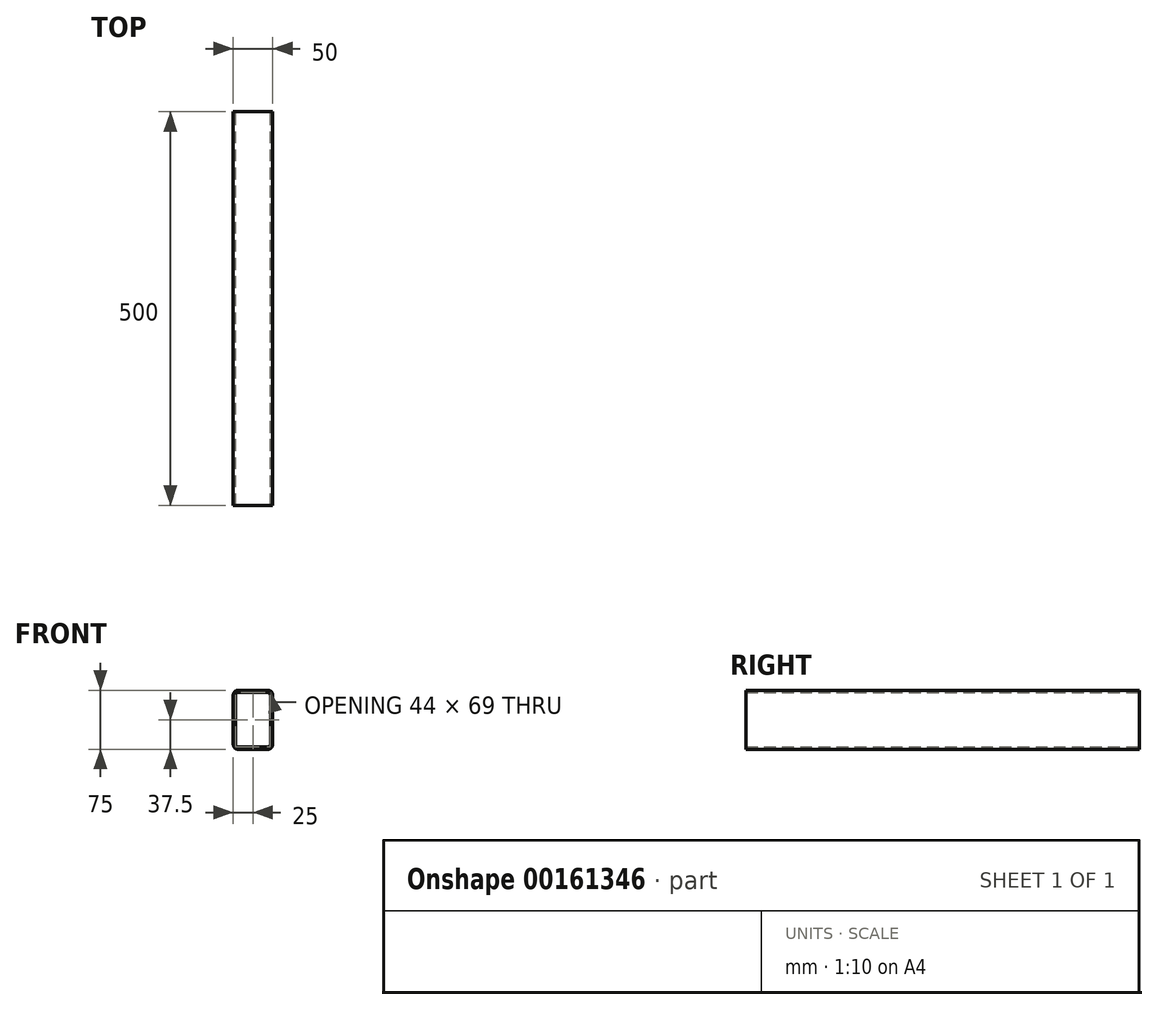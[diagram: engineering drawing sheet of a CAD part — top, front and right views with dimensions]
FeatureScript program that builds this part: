
annotation { "Feature Type Name" : "Feature", "Feature Type Description" : "" }
export const myFeature = defineFeature(function(context is Context, id is Id, definition is map)
    precondition{}
    {
        {
            var Q0;
            Q0=qCreatedBy(makeId("Front.planeOp"),FACE);
            var sketch = newSketch(context, id + "F0", { "sketchPlane" : qUnion([Q0])});
            skLineSegment(sketch, "E0.bottom", {"start": v(25, 37.5) * mm, "end": v(-25, 37.5) * mm});
            skLineSegment(sketch, "E0.top", {"start": v(25, -37.5) * mm, "end": v(-25, -37.5) * mm});
            skLineSegment(sketch, "E0.left", {"start": v(25, 37.5) * mm, "end": v(25, -37.5) * mm});
            skLineSegment(sketch, "E0.right", {"start": v(-25, 37.5) * mm, "end": v(-25, -37.5) * mm});
            skPoint(sketch, "E0.middle", {"position": v(0, 0) * mm});
            skSolve(sketch);
        }
        {
            var Q0;
            Q0=makeQuery(id+"F0.imprint","IMPRINT",FACE,{"disambiguationData":[TD([[makeQuery(id+"F0.imprint","IMPRINT",EDGE,{"derivedFrom":sQuery(id+"F0.wireOp",EDGE,"E0.bottom")}),1.0]])]});
            extrude(context, id + "F1", {"entities" : qUnion([Q0]), "depth" : 500 * mm});
        }
        {
            var Q0;
            Q0=makeQuery(id+"F1.opExtrude","SWEPT_EDGE",EDGE,{"disambiguationData":[OSD([sQuery(id+"F0.wireOp",EDGE,"E0.bottom"),sQuery(id+"F0.wireOp",EDGE,"E0.left")])]});
            var Q1;
            Q1=makeQuery(id+"F1.opExtrude","SWEPT_EDGE",EDGE,{"disambiguationData":[OSD([sQuery(id+"F0.wireOp",EDGE,"E0.bottom"),sQuery(id+"F0.wireOp",EDGE,"E0.right")])]});
            var Q2;
            Q2=makeQuery(id+"F1.opExtrude","SWEPT_EDGE",EDGE,{"disambiguationData":[OSD([sQuery(id+"F0.wireOp",EDGE,"E0.top"),sQuery(id+"F0.wireOp",EDGE,"E0.right")])]});
            var Q3;
            Q3=makeQuery(id+"F1.opExtrude","SWEPT_EDGE",EDGE,{"disambiguationData":[OSD([sQuery(id+"F0.wireOp",EDGE,"E0.top"),sQuery(id+"F0.wireOp",EDGE,"E0.left")])]});
            fillet(context, id + "F2", {"entities" : qUnion([Q0, Q1, Q2, Q3]), "radius" : 6 * mm, "tangentPropagation" : true, "allowEdgeOverflow" : false});
        }
        {
            var Q0;
            Q0=makeQuery(id+"F1.opExtrude","CAP_FACE",FACE,{"disambiguationData":[OSD([sQuery(id+"F0.wireOp",EDGE,"E0.bottom"),sQuery(id+"F0.wireOp",EDGE,"E0.top"),sQuery(id+"F0.wireOp",EDGE,"E0.left"),sQuery(id+"F0.wireOp",EDGE,"E0.right")])],"isStart":false});
            var Q1;
            Q1=makeQuery(id+"F1.opExtrude","CAP_FACE",FACE,{"disambiguationData":[OSD([sQuery(id+"F0.wireOp",EDGE,"E0.bottom"),sQuery(id+"F0.wireOp",EDGE,"E0.top"),sQuery(id+"F0.wireOp",EDGE,"E0.left"),sQuery(id+"F0.wireOp",EDGE,"E0.right")])],"isStart":true});
            shell(context, id + "F3", {"entities" : qUnion([Q0, Q1]), "thickness" : 3 * mm});
        }
    });
